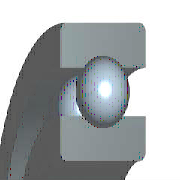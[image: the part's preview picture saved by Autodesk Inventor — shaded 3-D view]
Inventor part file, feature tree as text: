
AUTODESK INVENTOR PART (.ipt)
format: ipt  version: 2025 (Build 290162000, 162)  size: 284,672 bytes
history: native  units: mm (DEFAULTED — no unit token found)
features: other x1, pattern_circular x1
ambient origin geometry x8: Origin, YZ Plane, XZ Plane, XY Plane, X Axis, Y Axis, Z Axis, Center Point
bodies: Solid1 (feature_tree)
feature tree (2):
  other  "轴承体"
  pattern_circular  "IDS_ARRAYBALL[SIMPL:T]"  Angle=90.0deg  [1 undecoded]
note: 1 required parameter value undecoded (feature->parameter linkage not recoverable at this tier; creation-order binding heuristic only, values carry confidence <= 0.55)
